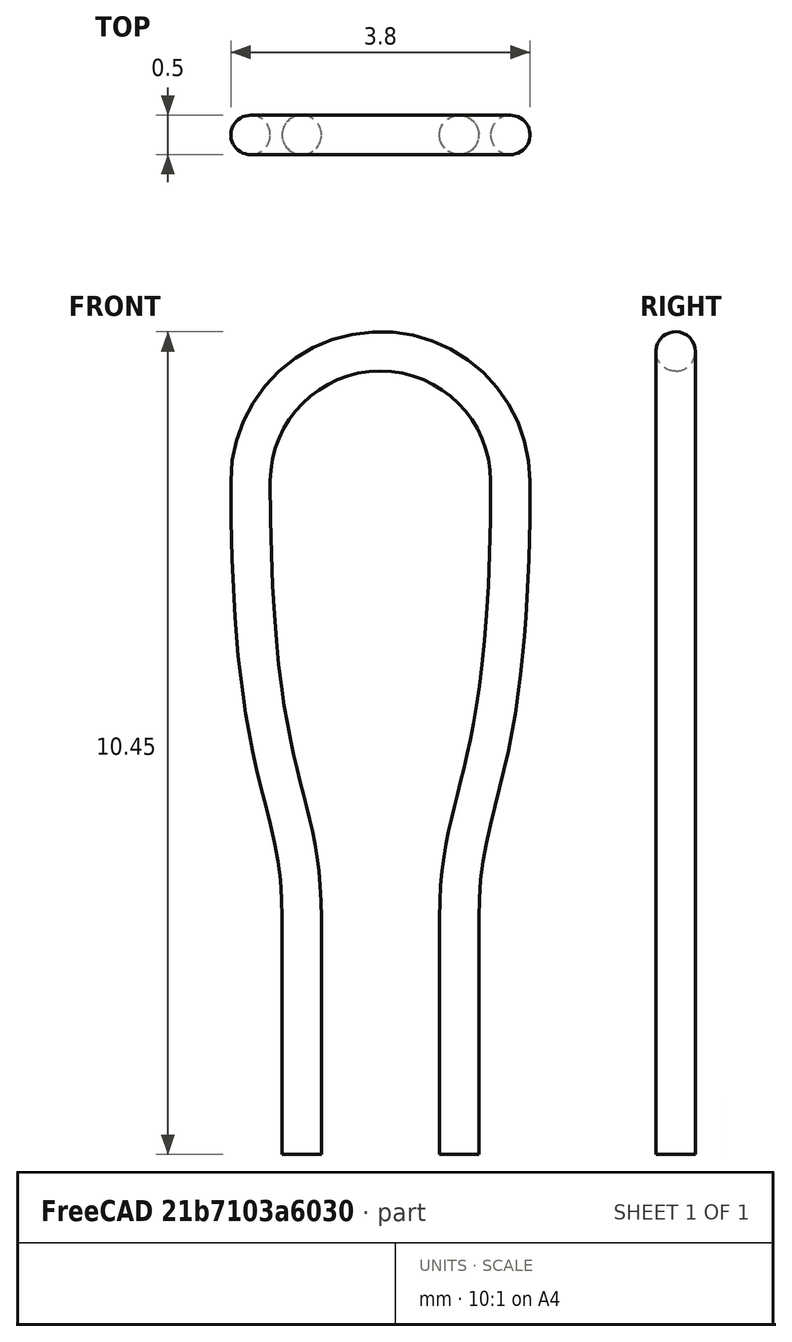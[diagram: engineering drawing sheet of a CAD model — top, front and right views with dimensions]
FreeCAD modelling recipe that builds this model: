
FCSTD DOCUMENT  (FreeCAD 0.17R12018 (Git))
Label: Test_Point_Loop_D3.80mm_Drill2.5mm
License: All rights reserved
LicenseURL: http://en.wikipedia.org/wiki/All_rights_reserved
objects: Sketcher::SketchObject×2, Spreadsheet::Sheet×1, PartDesign::AdditivePipe×1, PartDesign::Body×1, App::Part×1
note: 5 computed .brp shape members not serialized (recipe doc carries the construction recipe); baked Part::Feature solids carry a one-line shape summary decoded from their .brp

FEATURE [Spreadsheet::Sheet] Spreadsheet  label="dims"
  cells = A1="DWire"; B1(DWire)=0.5; A2="DLoop"; B2(DLoop)=3.7999999999999998; A3="Spacer"; B3(Spacer)=0; A4="DSpacer"; B4(DSpacer)=3; A5="Lall"; B5(Lall)=10.199999999999999; A6="Ddrill"; B6(Ddrill)=2.5; A7="Lbottom"; B7(Lbottom)=3
FEATURE [Sketcher::SketchObject] Sketch001
  MapMode = 5
  Placement = pos=(0,0,0) rot=(1,0,0;1.5708rad)
  expr: Constraints[63] = (dims.DLoop - dims.DWire) / 2
  expr: Constraints[28] = dims.Lall - (dims.DLoop - dims.DWire) / 2
  expr: Constraints[27] = (dims.DLoop - dims.DWire) / 2
  expr: Constraints[30] = dims.Lbottom
  expr: Constraints[32] = dims.Spacer
  expr: Constraints[33] = dims.Ddrill - dims.DWire
  expr: Constraints[34] = (dims.Ddrill - dims.DWire) / 2
  sketch-geometry (25):
    g0: LineSegment StartX=-1 StartY=-3 StartZ=0 EndX=-1 EndY=-1.22871e-07 EndZ=0
    g1: LineSegment StartX=1 StartY=-2.55641e-07 StartZ=0 EndX=1 EndY=-3 EndZ=0
    g2: ArcOfCircle CenterX=0 CenterY=5.55 CenterZ=0 NormalX=0 NormalY=0 NormalZ=1 Radius=1.65 StartAngle=6.28319 EndAngle=9.42478
    g3: LineSegment [constr] StartX=-1.65 StartY=5.55 StartZ=0 EndX=1.65 EndY=5.55 EndZ=0
    g4: LineSegment [constr] StartX=-1.65 StartY=-2.36463e-07 StartZ=0 EndX=1.65 EndY=-2.36463e-07 EndZ=0
    g5: LineSegment [constr] StartX=1.65 StartY=5.55 StartZ=0 EndX=1.65 EndY=-2.36463e-07 EndZ=0
    g6: LineSegment [constr] StartX=-1.65 StartY=-2.36463e-07 StartZ=0 EndX=-1.65 EndY=5.55 EndZ=0
    g7: LineSegment [constr] StartX=-1 StartY=-1.22871e-07 StartZ=0 EndX=-1 EndY=1.65 EndZ=0
    g8: LineSegment [constr] StartX=1 StartY=-2.55641e-07 StartZ=0 EndX=1 EndY=1.65 EndZ=0
    g9: LineSegment [constr] StartX=-1.65 StartY=1.65 StartZ=0 EndX=1.65 EndY=1.65 EndZ=0
    g10: LineSegment [constr] StartX=1 StartY=1.65 StartZ=0 EndX=1 EndY=5.55 EndZ=0
    g11-g14: Circle [constr] x4 (B-spline internal-alignment scaffolding for g15; pole/knot coordinates omitted)
    g15: BSplineCurve PolesCount=4 KnotsCount=2 Degree=3 IsPeriodic=0
    g16: GeomPoint [constr] X=-1 Y=-1.22871e-07 Z=0
    g17: GeomPoint [constr] X=-1.65 Y=5.55 Z=0
    g18-g21: Circle [constr] x4 (B-spline internal-alignment scaffolding for g22; pole/knot coordinates omitted)
    g22: BSplineCurve PolesCount=4 KnotsCount=2 Degree=3 IsPeriodic=0
    g23: GeomPoint [constr] X=1 Y=-2.55641e-07 Z=0
    g24: GeomPoint [constr] X=1.65 Y=5.55 Z=0
  constraints (58):
    c: Vertical(g0)
    c: Vertical(g1)
    c: Coincident(g3,g2)
    c: Horizontal(g3)
    c: PointOnObject(g2,g3)
    c: Coincident(g3,g2)
    c: PointOnObject(g2,g-2)
    c: Horizontal(g4)
    c: Coincident(g5,g2)
    c: Coincident(g5,g4)
    c: Coincident(g6,g4)
    c: Coincident(g6,g2)
    c: PointOnObject(g0,g4)
    c: PointOnObject(g1,g4)
    c: Vertical(g6)
    c: Vertical(g5)
    c: Coincident(g7,g0)
    c: Vertical(g7)
    c: Coincident(g8,g1)
    c: Vertical(g8)
    c: PointOnObject(g9,g6)
    c: PointOnObject(g9,g5)
    c: Horizontal(g9)
    c: PointOnObject(g7,g9)
    c: PointOnObject(g8,g9)
    c: PointOnObject(g10,g3)
    c: Vertical(g10)
    c: Radius(g2) = 1.65
    c: DistanceY(g1,g2) = 8.55
    c: DistanceY(g1,g0) = 0
    c: DistanceY(g0,g-1) = 3
    c: Coincident(g10,g8)
    c: DistanceY(g-1,g0) = 0
    c: DistanceX(g0,g1) = 2
    c: DistanceX(g0,g-1) = 1
    c: Coincident(g11,g0)
    c: Radius(g11) = 0
    c: Equal(g11,g12)
    c: Coincident(g12,g7)
    c: Equal(g11,g13)
    c: Coincident(g13,g9)
    c: Equal(g11,g14)
    c: Coincident(g14,g2)
    c: InternalAlignment(g11-g14 -> g15) x4
    c: InternalAlignment(g16,g15)
    c: InternalAlignment(g17,g15)
    c: Coincident(g18,g1)
    c: Radius(g18) = 0
    c: Equal(g18,g19)
    c: Coincident(g19,g8)
    c: Equal(g18,g20)
    c: Coincident(g20,g9)
    c: Equal(g18,g21)
    c: Coincident(g21,g2)
    c: InternalAlignment(g18-g21 -> g22) x4
    c: InternalAlignment(g23,g22)
    c: InternalAlignment(g24,g22)
    c: DistanceY(g4,g9) = 1.65
FEATURE [Sketcher::SketchObject] Sketch
  MapMode = 5
  Placement = pos=(0,0,-3) rot=(0,0,1;0rad)
  expr: Constraints[2] = (dims.Ddrill - dims.DWire) / 2
  expr: Constraints[1] = dims.DWire / 2
  sketch-geometry (1):
    g0: Circle CenterX=-1 CenterY=0 CenterZ=0 NormalX=0 NormalY=0 NormalZ=1 Radius=0.25
  constraints (3):
    c: PointOnObject(g0,g-1)
    c: Radius(g0) = 0.25
    c: DistanceX(g0,g-1) = 1
FEATURE [PartDesign::AdditivePipe] AdditivePipe
  AuxilleryCurvelinear = true
  AuxillerySpineTangent = false
  Binormal = (0,0,0)
  Mode = 0
  Placement = pos=(0,0,-3) rot=(0,0,1;0rad)
  Profile = -> Sketch
  Spine = -> Sketch001 [Edge1,Edge2,Edge3,Edge4,Edge5]
  SpineTangent = false
  Transformation = 0
  Transition = 0
FEATURE [PartDesign::Body] Body  label="Test_Point_Loop_D3.80mm_Drill2.5mm"
  Group = -> [Sketch,Sketch001,AdditivePipe]
  Origin = -> Origin002
  Tip = -> AdditivePipe
FEATURE [App::Part] Part  label="group"
  Group = -> [Body]
  License = CC BY 3.0
  LicenseURL = http://creativecommons.org/licenses/by/3.0/
  Origin = -> Origin
